# Revit family: oventrop_av-9_1183703-06rfa
name_source: partatom
category: Арматура трубопроводов
revit_build: Autodesk Revit 2017 (Build: 20160225_1515(x64)
units: mm (PartAtom-declared; Revit-internal decimal feet)

## family parameters
Всегда вертикально = Да
Заголовок OmniClass = Adjusting/Controlling Valves for Liquid Services
На основе рабочей плоскости = Нет
Номер OmniClass = 23.65.55.14.17
Общий = Нет
При загрузке вырезать с полостями = Нет
Размер круглого соединителя = Использовать диаметр
Тип детали = Нормальный

## types (3) — shared parameters
Article Description = Thermostatic radiator valve, angle pattern
Brass = Color RGB 168-128-048
Cast Iron = Color RGB 140-140-140
Custom = Нет
EMCS Version = 2.0
ETIM Article Class = EC010136
Family Version = 10.14
IFCExportAs = IfcValveType
IFCExportType = REGULATING
Kvs Value = 0.67
MEPcontent Class = VALVE_RADIATOR
Manufacturer URL = http://www.oventrop.de
Pressure Stage = 10.0 Па
Product Line = Oventrop
Revit Version = 2015
Use Nominal Diameter = Да
Valve Insert Diameter = 30 мм
Изготовитель = Oventrop
Описание = Thermostatic radiator valve, angle pattern

## per-type parameters (varying)
- DN 10: Bottom Height=22 мм; Bottom Part Radius=10 мм; Connection Piece Radius=8 мм; Copper Connection Diameter=12 мм; Copper Connection Radius=6 мм; GTIN=04026755407259; Height=63.5 мм; Horizontal Nut Diameter=27 мм; Horizontal Nut Height=13.5 мм; Horizontal Nut Position=20 мм; Length=67 мм; Manufacturer Art. No.=1183703; Middle Section Radius=10 мм; Rind Height=17.16 мм; Ring Position=19 мм; Ring Radius=20.05 мм; Ring Vizibility=Нет; Thread Connection Diameter=9.5 мм; Thread Connection Nominal Diameter=9.5 мм; Thread Connection Nominal Radius=4.75 мм; Thread Connection Outer Diameter=17.2 мм; Thread Connection Outer Radius=8.6 мм; URL=http://file-system.ru; Valve Body Height=21.5 мм; Valve Body Radius=12 мм; Vertical Nut Diameter=22 мм; Vertical Nut Height=12 мм
- DN 15: Bottom Height=26 мм; Bottom Part Radius=11.5 мм; Connection Piece Radius=10.5 мм; Copper Connection Diameter=15 мм; Copper Connection Radius=7.5 мм; GTIN=04026755407266; Height=69 мм; Horizontal Nut Diameter=30 мм; Horizontal Nut Height=15 мм; Horizontal Nut Position=23 мм; Length=73 мм; Manufacturer Art. No.=1183704; Middle Section Radius=11 мм; Rind Height=14 мм; Ring Position=23 мм; Ring Radius=13 мм; Ring Vizibility=Да; Thread Connection Diameter=12.7 мм; Thread Connection Nominal Diameter=12.7 мм; Thread Connection Nominal Radius=6.35 мм; Thread Connection Outer Diameter=21.3 мм; Thread Connection Outer Radius=10.65 мм; URL=www.stabiplan.com; Valve Body Height=22 мм; Valve Body Radius=12.5 мм; Vertical Nut Diameter=26 мм; Vertical Nut Height=14 мм
- DN 20: Bottom Height=29 мм; Bottom Part Radius=13 мм; Connection Piece Radius=13 мм; Copper Connection Diameter=22 мм; Copper Connection Radius=11 мм; GTIN=04026755407273; Height=69 мм; Horizontal Nut Diameter=37 мм; Horizontal Nut Height=16.5 мм; Horizontal Nut Position=24.5 мм; Length=81 мм; Manufacturer Art. No.=1183706; Middle Section Radius=12.63 мм; Rind Height=14 мм; Ring Position=27 мм; Ring Radius=15 мм; Ring Vizibility=Да; Thread Connection Diameter=19 мм; Thread Connection Nominal Diameter=19 мм; Thread Connection Nominal Radius=9.5 мм; Thread Connection Outer Diameter=26.9 мм; Thread Connection Outer Radius=13.45 мм; URL=www.stabiplan.com; Valve Body Height=19 мм; Valve Body Radius=12.5 мм; Vertical Nut Diameter=32 мм; Vertical Nut Height=16 мм

note: column(s) folded — value = type name in every type: Article Type, Группа модели

## geometry (parser evidence)
native form markers: Sweep x8
no freeform markers — native parametric forms only
